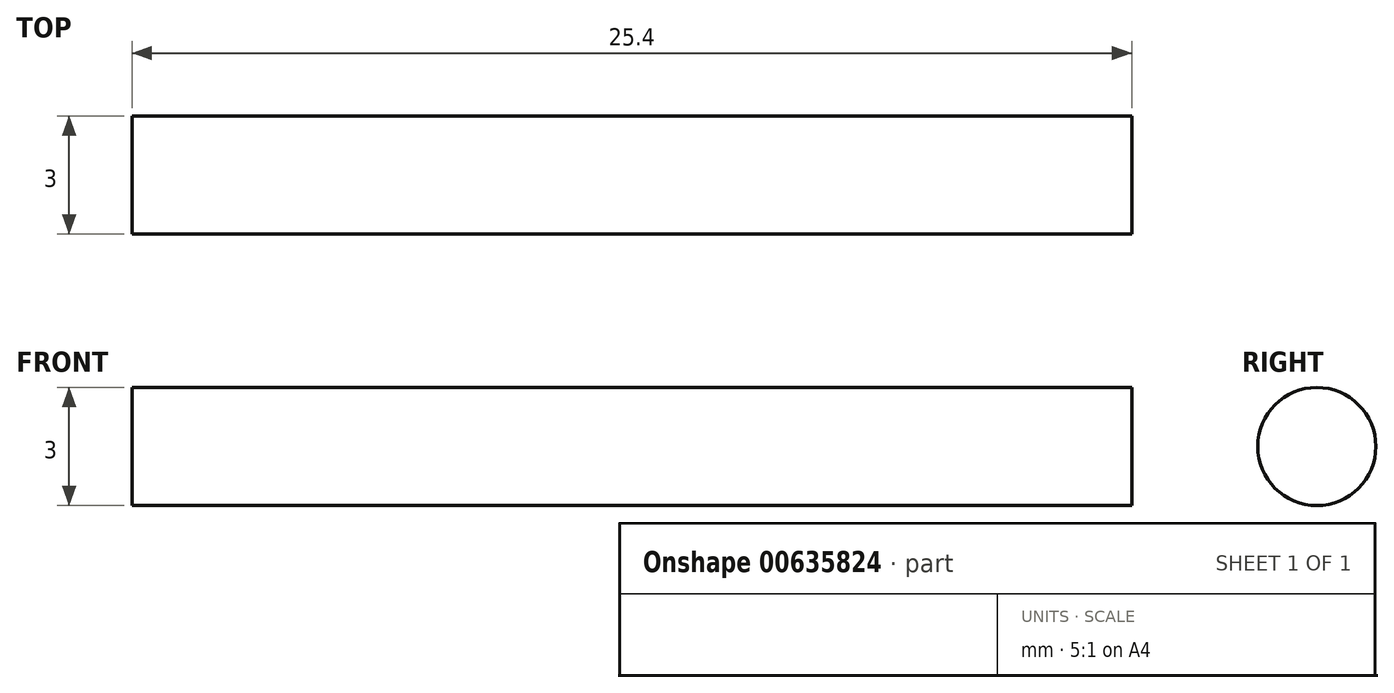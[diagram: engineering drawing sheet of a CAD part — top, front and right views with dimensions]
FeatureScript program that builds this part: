
annotation { "Feature Type Name" : "Feature", "Feature Type Description" : "" }
export const myFeature = defineFeature(function(context is Context, id is Id, definition is map)
    precondition{}
    {
        {
            var Q0;
            Q0=qCreatedBy(makeId("Right.planeOp"),FACE);
            var sketch = newSketch(context, id + "F0", { "sketchPlane" : qUnion([Q0])});
            skCircle(sketch, "E0", {"center": v(0, 0) * mm, "radius": 1.5 * mm});
            skSolve(sketch);
        }
        {
            var Q0;
            Q0=makeQuery(id+"F0.imprint","IMPRINT",FACE,{"disambiguationData":[TD([[makeQuery(id+"F0.imprint","IMPRINT",EDGE,{"derivedFrom":sQuery(id+"F0.wireOp",EDGE,"E0")}),1.0]])]});
            extrude(context, id + "F1", {"entities" : qUnion([Q0]), "depth" : 25.4 * mm, "offsetDistance" : 25.4 * mm});
        }
    });
